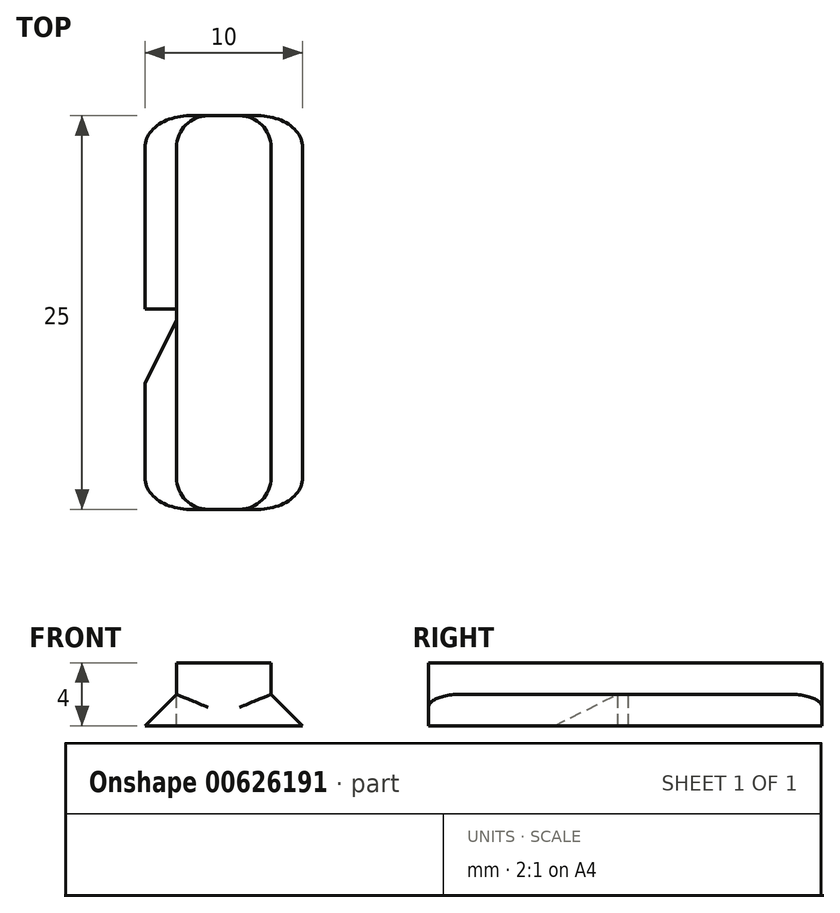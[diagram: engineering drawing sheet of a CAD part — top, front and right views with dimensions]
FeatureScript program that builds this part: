
annotation { "Feature Type Name" : "Feature", "Feature Type Description" : "" }
export const myFeature = defineFeature(function(context is Context, id is Id, definition is map)
    precondition{}
    {
        {
            var Q0;
            Q0=qCreatedBy(makeId("Front.planeOp"),FACE);
            var sketch = newSketch(context, id + "F0", { "sketchPlane" : qUnion([Q0])});
            skLineSegment(sketch, "E0", {"start": v(0, 0) * mm, "end": v(3, 0) * mm});
            skLineSegment(sketch, "E1", {"start": v(0, 0) * mm, "end": v(-3, 0) * mm});
            skLineSegment(sketch, "E2", {"start": v(-3, 0) * mm, "end": v(-3, -1) * mm});
            skLineSegment(sketch, "E3", {"start": v(-5, -3) * mm, "end": v(5, -3) * mm});
            skLineSegment(sketch, "E4", {"start": v(3, -1) * mm, "end": v(3, 0) * mm});
            skLineSegment(sketch, "E5", {"start": v(-3, -1) * mm, "end": v(-5, -3) * mm});
            skLineSegment(sketch, "E6", {"start": v(5, -3) * mm, "end": v(3, -1) * mm});
            skLineSegment(sketch, "E7", {"start": v(3, -1) * mm, "end": v(5, -1) * mm, "construction": true});
            skLineSegment(sketch, "E8", {"start": v(5, -1) * mm, "end": v(5, -3) * mm, "construction": true});
            skLineSegment(sketch, "E9", {"start": v(-5, -3) * mm, "end": v(-5, -1) * mm, "construction": true});
            skLineSegment(sketch, "E10", {"start": v(-5, -1) * mm, "end": v(-3, -1) * mm, "construction": true});
            skLineSegment(sketch, "E11", {"start": v(-3, 0) * mm, "end": v(-3, 1) * mm});
            skLineSegment(sketch, "E12", {"start": v(-3, 1) * mm, "end": v(3, 1) * mm});
            skLineSegment(sketch, "E13", {"start": v(3, 1) * mm, "end": v(3, 0) * mm});
            skSolve(sketch);
        }
        {
            var Q0;
            Q0=makeQuery(id+"F0.imprint","IMPRINT",FACE,{"disambiguationData":[TD([[makeQuery(id+"F0.imprint","IMPRINT",EDGE,{"derivedFrom":sQuery(id+"F0.wireOp",EDGE,"E0")}),-1.0]])]});
            var Q1;
            Q1=makeQuery(id+"F0.imprint","IMPRINT",FACE,{"disambiguationData":[TD([[makeQuery(id+"F0.imprint","IMPRINT",EDGE,{"derivedFrom":sQuery(id+"F0.wireOp",EDGE,"E0")}),1.0]])]});
            extrude(context, id + "F1", {"entities" : qUnion([Q0, Q1]), "depth" : 25 * mm, "offsetDistance" : 25 * mm});
        }
        {
            var Q0;
            Q0=makeQuery(id+"F1.opExtrude","CAP_EDGE",EDGE,{"disambiguationData":[OSD([sQuery(id+"F0.wireOp",EDGE,"E2"),sQuery(id+"F0.wireOp",EDGE,"E11")])],"isStart":false});
            var Q1;
            Q1=makeQuery(id+"F1.opExtrude","CAP_EDGE",EDGE,{"disambiguationData":[OSD([sQuery(id+"F0.wireOp",EDGE,"E5")])],"isStart":false});
            var Q2;
            Q2=makeQuery(id+"F1.opExtrude","CAP_EDGE",EDGE,{"disambiguationData":[OSD([sQuery(id+"F0.wireOp",EDGE,"E6")])],"isStart":false});
            var Q3;
            Q3=makeQuery(id+"F1.opExtrude","CAP_EDGE",EDGE,{"disambiguationData":[OSD([sQuery(id+"F0.wireOp",EDGE,"E4"),sQuery(id+"F0.wireOp",EDGE,"E13")])],"isStart":false});
            var Q4;
            Q4=makeQuery(id+"F1.opExtrude","CAP_EDGE",EDGE,{"disambiguationData":[OSD([sQuery(id+"F0.wireOp",EDGE,"E5")])],"isStart":true});
            var Q5;
            Q5=makeQuery(id+"F1.opExtrude","CAP_EDGE",EDGE,{"disambiguationData":[OSD([sQuery(id+"F0.wireOp",EDGE,"E4"),sQuery(id+"F0.wireOp",EDGE,"E13")])],"isStart":true});
            var Q6;
            Q6=makeQuery(id+"F1.opExtrude","CAP_EDGE",EDGE,{"disambiguationData":[OSD([sQuery(id+"F0.wireOp",EDGE,"E6")])],"isStart":true});
            var Q7;
            Q7=makeQuery(id+"F1.opExtrude","CAP_EDGE",EDGE,{"disambiguationData":[OSD([sQuery(id+"F0.wireOp",EDGE,"E2"),sQuery(id+"F0.wireOp",EDGE,"E11")])],"isStart":true});
            fillet(context, id + "F2", {"entities" : qUnion([Q0, Q1, Q2, Q3, Q4, Q5, Q6, Q7]), "radius" : 2 * mm, "tangentPropagation" : true, "allowEdgeOverflow" : false});
        }
        {
            var Q0;
            Q0=makeQuery(id+"F1.opExtrude","SWEPT_FACE",FACE,{"disambiguationData":[OSD([sQuery(id+"F0.wireOp",EDGE,"E12")])]});
            var sketch = newSketch(context, id + "F3", { "sketchPlane" : qUnion([Q0])});
            skLineSegment(sketch, "E14", {"start": v(0, 0) * mm, "end": v(0, -25) * mm, "construction": true});
            skLineSegment(sketch, "E15", {"start": v(-3, -12.5) * mm, "end": v(-7.48, -12.5) * mm});
            skLineSegment(sketch, "E16", {"start": v(-7.48, -12.5) * mm, "end": v(-7.48, -19.5) * mm});
            skLineSegment(sketch, "E17", {"start": v(-3, -12.5) * mm, "end": v(-6.47, -19.5) * mm});
            skLineSegment(sketch, "E18", {"start": v(-7.48, -19.5) * mm, "end": v(-6.47, -19.5) * mm});
            skLineSegment(sketch, "E19.0", {"start": v(-2.66, -12.3) * mm, "end": v(-7.69, -12.3) * mm});
            skLineSegment(sketch, "E19.1", {"start": v(-2.66, -12.3) * mm, "end": v(-6.34, -19.7) * mm});
            skLineSegment(sketch, "E19.2", {"start": v(-7.69, -19.7) * mm, "end": v(-6.34, -19.7) * mm});
            skLineSegment(sketch, "E19.3", {"start": v(-7.69, -12.3) * mm, "end": v(-7.69, -19.7) * mm});
            skLineSegment(sketch, "E20.0", {"start": v(-5, -23) * mm, "end": v(-5, -2) * mm, "construction": true});
            skPoint(sketch, "E21", {"position": v(-5, -12.3) * mm});
            skPoint(sketch, "E22", {"position": v(-5, -16.53) * mm});
            skSolve(sketch);
        }
        {
            var Q0;
            {var subQ1=sQuery(id+"F3.wireOp",EDGE,"E15");Q0=makeQuery(id+"F3.imprint","IMPRINT",FACE,{"disambiguationData":[TD([[makeQuery(id+"F3.imprint","IMPRINT",EDGE,{"derivedFrom":subQ1}),-1.0]])]});}
            var Q1;
            Q1=makeQuery(id+"F3.imprint","IMPRINT",FACE,{"disambiguationData":[TD([[makeQuery(id+"F3.imprint","IMPRINT",EDGE,{"derivedFrom":sQuery(id+"F3.wireOp",EDGE,"E15")}),1.0]])]});
            extrude(context, id + "F4", {"entities" : qUnion([Q0, Q1]), "operationType" : NewBodyOperationType.REMOVE, "oppositeDirection" : true, "depth" : 25 * mm, "offsetDistance" : 25 * mm});
        }
    });
